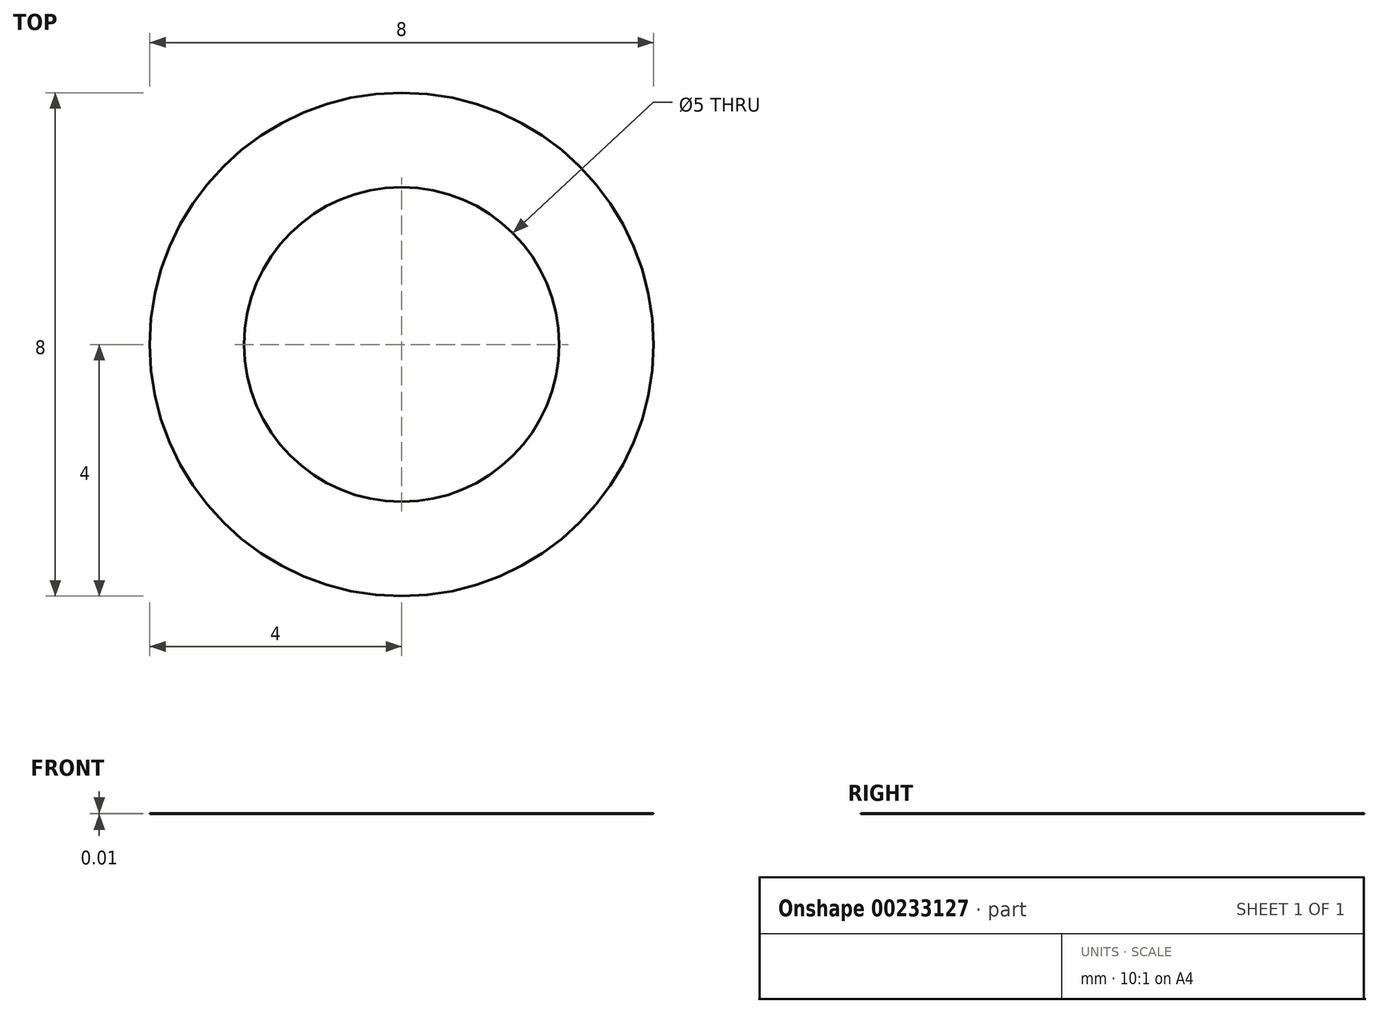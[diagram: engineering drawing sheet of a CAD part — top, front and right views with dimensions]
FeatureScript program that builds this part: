
annotation { "Feature Type Name" : "Feature", "Feature Type Description" : "" }
export const myFeature = defineFeature(function(context is Context, id is Id, definition is map)
    precondition{}
    {
        {
            var Q0;
            Q0=qCreatedBy(makeId("Top.planeOp"),FACE);
            var sketch = newSketch(context, id + "F0", { "sketchPlane" : qUnion([Q0])});
            skCircle(sketch, "E0", {"center": v(0, 0) * mm, "radius": 4 * mm});
            skCircle(sketch, "E1", {"center": v(0, 0) * mm, "radius": 2.5 * mm});
            skSolve(sketch);
        }
        {
            var Q0;
            Q0 = qSketchRegion(id + "F0", true);
            extrude(context, id + "F1", {"entities" : qUnion([Q0]), "depth" : 1 / 101.6 * mm});
        }
    });
